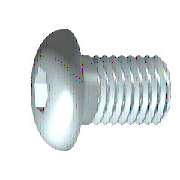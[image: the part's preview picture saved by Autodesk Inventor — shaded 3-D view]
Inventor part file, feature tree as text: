
AUTODESK INVENTOR PART (.ipt)
format: ipt  version: 2015 (Build 190159000, 159)  size: 193,024 bytes
history: native  units: mm (DEFAULTED — no unit token found)
features: sketch x2, extrude x1, plane x1, fillet x1
ambient origin geometry x7: Origin, YZ Plane, XY Plane, X Axis, Y Axis, Z Axis, Center Point
bodies: Solid1 (feature_tree), Body (feature_tree)
feature tree (5):
  extrude  "Slot"  Depth=1.8542mm
  plane  "Work Plane1"
  fillet  "Fillet2"  Radius=1.8542mm
  sketch  "Sketch1"  dims[d1=11.10976mm d2=1.59014mm d3=1.8542mm]
  sketch  "Sketch2"  dims[d4=1.1176mm d5=60.0deg d6=3.5052mm d7=3.5052mm d8=2.287693mm d9=6.6548mm d10=90.0deg d11=10.0mm d12=0.0mm d13=11.10976mm d14=0.0mm d15=0.486918mm d16=0.486918mm d17=1.6002mm d19=0.0mm d26=12.7mm d27=45.0deg d28=0.0mm d29=0.0mm d30=0.1mm]
